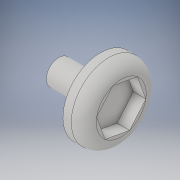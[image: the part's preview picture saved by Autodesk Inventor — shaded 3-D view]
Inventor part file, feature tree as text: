
AUTODESK INVENTOR PART (.ipt)
format: ipt  version: 2019 (Build 230136000, 136)  size: 144,384 bytes
history: native  units: mm
features: sketch x2, projected_geometry x2, other x1, revolve x1, fillet x1, extrude x1
ambient origin geometry x8: Origin, YZ Plane, XZ Plane, XY Plane, X Axis, Y Axis, Z Axis, Center Point
bodies: Body1 (feature_tree)
feature tree (8):
  other  "Bryła1"
  revolve  "Obrót1"
  fillet  "Zaokrąglenie1"  Radius=0.3mm
  extrude  "Wyciągnięcie proste1"  Depth=1.0mm
  sketch  "Szkic1"
  sketch  "Szkic2"
  projected_geometry  "Pętla rzutowana1"
  projected_geometry  "Pętla rzutowana2"
